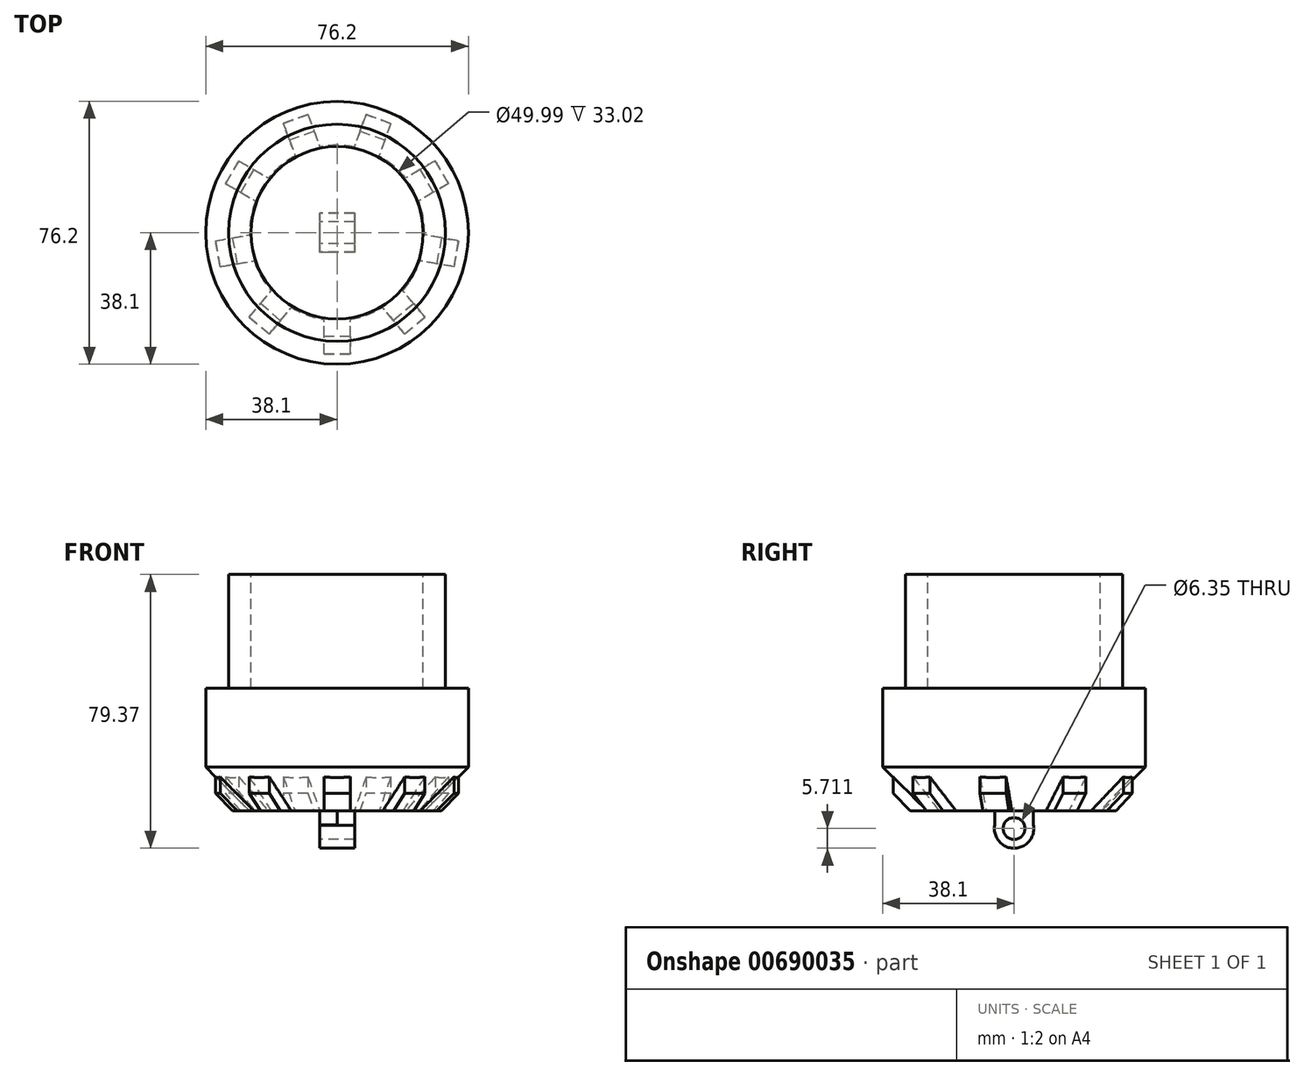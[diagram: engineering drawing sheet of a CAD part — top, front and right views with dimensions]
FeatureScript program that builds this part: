
annotation { "Feature Type Name" : "Feature", "Feature Type Description" : "" }
export const myFeature = defineFeature(function(context is Context, id is Id, definition is map)
    precondition{}
    {
        {
            var Q0;
            Q0=qCreatedBy(makeId("Top.planeOp"),FACE);
            cPlane(context, id + "F0", {"entities" : qUnion([Q0]), "cplaneType" : CPlaneType.OFFSET, "offset" : 83.28 * mm, "oppositeDirection" : true, "width" : 152.4 * mm, "height" : 152.4 * mm});
        }
        {
            var Q0;
            Q0=qCreatedBy(id+"F0.planeOp",FACE);
            cPlane(context, id + "F1", {"entities" : qUnion([Q0]), "cplaneType" : CPlaneType.OFFSET, "offset" : 15.6 * mm, "oppositeDirection" : true, "width" : 152.4 * mm, "height" : 152.4 * mm});
        }
        {
            var Q0;
            Q0=qCreatedBy(id+"F1.planeOp",FACE);
            var sketch = newSketch(context, id + "F2", { "sketchPlane" : qUnion([Q0])});
            skCircle(sketch, "E0", {"center": v(0, 0) * mm, "radius": 25 * mm});
            skCircle(sketch, "E1", {"center": v(0, 0) * mm, "radius": 31.46 * mm});
            skSolve(sketch);
        }
        {
            var Q0;
            Q0=makeQuery(id+"F2.imprint","IMPRINT",FACE,{"disambiguationData":[TD([[makeQuery(id+"F2.imprint","IMPRINT",EDGE,{"derivedFrom":sQuery(id+"F2.wireOp",EDGE,"E0")}),-1.0]])]});
            extrude(context, id + "F3", {"entities" : qUnion([Q0]), "oppositeDirection" : true, "depth" : 33.02 * mm, "offsetDistance" : 25.4 * mm});
        }
        {
            var Q0;
            Q0=makeQuery(id+"F3.opExtrude","CAP_FACE",FACE,{"disambiguationData":[OSD([sQuery(id+"F2.wireOp",EDGE,"E0"),sQuery(id+"F2.wireOp",EDGE,"E1")])],"isStart":false});
            var sketch = newSketch(context, id + "F4", { "sketchPlane" : qUnion([Q0])});
            skCircle(sketch, "E2", {"center": v(0, 0) * mm, "radius": 38.1 * mm});
            skSolve(sketch);
        }
        {
            var Q0;
            Q0=makeQuery(id+"F4.imprint","IMPRINT",FACE,{"disambiguationData":[TD([[makeQuery(id+"F4.imprint","IMPRINT",EDGE,{"derivedFrom":sQuery(id+"F4.wireOp",EDGE,"E2")}),1.0]])]});
            var Q1;
            Q1=makeQuery(id+"F4.imprint","IMPRINT",FACE,{"disambiguationData":[TD([[makeQuery(id+"F4.imprint","IMPRINT",EDGE,{"derivedFrom":makeQuery(id+"F3.opExtrude","CAP_EDGE",EDGE,{"disambiguationData":[OSD([sQuery(id+"F2.wireOp",EDGE,"E0")])],"isStart":false})}),1.0]])]});
            var Q2;
            Q2=makeQuery(id+"F4.imprint","IMPRINT",FACE,{"disambiguationData":[TD([[makeQuery(id+"F4.imprint","IMPRINT",EDGE,{"derivedFrom":makeQuery(id+"F3.opExtrude","CAP_EDGE",EDGE,{"disambiguationData":[OSD([sQuery(id+"F2.wireOp",EDGE,"E0")])],"isStart":false})}),-1.0]])]});
            extrude(context, id + "F5", {"entities" : qUnion([Q0, Q1, Q2]), "operationType" : NewBodyOperationType.ADD, "depth" : 35.56 * mm, "offsetDistance" : 25.4 * mm});
        }
        {
            var Q0;
            Q0=makeQuery(id+"F5.opExtrude","CAP_EDGE",EDGE,{"disambiguationData":[OSD([sQuery(id+"F4.wireOp",EDGE,"E2")])],"isStart":false});
            chamfer(context, id + "F6", {"entities" : qUnion([Q0]), "width" : 12.7 * mm, "tangentPropagation" : true});
        }
        {
            var Q0;
            Q0=makeQuery(id+"F5.opExtrude","CAP_FACE",FACE,{"disambiguationData":[OSD([sQuery(id+"F4.wireOp",EDGE,"E2")])],"isStart":false});
            var sketch = newSketch(context, id + "F7", { "sketchPlane" : qUnion([Q0])});
            skSolve(sketch);
        }
        {
            var Q0;
            {var subQ0=sQuery(id+"F4.wireOp",EDGE,"E2");Q0=makeQuery(id+"F7.imprint","IMPRINT",FACE,{"disambiguationData":[TD([[makeQuery(id+"F7.imprint","IMPRINT",EDGE,{"derivedFrom":makeQuery(id+"F6.opChamfer","BLEND_EDGE",EDGE,{"blendedFrom":[makeQuery(id+"F5.opExtrude","CAP_EDGE",EDGE,{"disambiguationData":[OSD([subQ0])],"isStart":false}),makeQuery(id+"F5.opExtrude","CAP_FACE",FACE,{"disambiguationData":[OSD([subQ0])],"isStart":false})],"blendedInto":[makeQuery(id+"F5.opExtrude","CAP_FACE",FACE,{"disambiguationData":[OSD([subQ0])],"isStart":false})]})}),1.0]])]});}
            var sketch = newSketch(context, id + "F8", { "sketchPlane" : qUnion([Q0])});
            skLineSegment(sketch, "E3.bottom", {"start": v(3.81, 23.68) * mm, "end": v(-3.81, 23.68) * mm});
            skLineSegment(sketch, "E3.top", {"start": v(3.81, 35.11) * mm, "end": v(-3.81, 35.11) * mm});
            skLineSegment(sketch, "E3.left", {"start": v(3.8, 35.11) * mm, "end": v(3.81, 23.68) * mm});
            skLineSegment(sketch, "E3.right", {"start": v(-3.81, 35.11) * mm, "end": v(-3.81, 23.68) * mm});
            skPoint(sketch, "E3.middle", {"position": v(0, 29.4) * mm});
            skLineSegment(sketch, "E4.1.0", {"start": v(-19.65, 29.35) * mm, "end": v(-12.3, 20.6) * mm});
            skPoint(sketch, "E4.1.1", {"position": v(-18.9, 22.52) * mm});
            skLineSegment(sketch, "E4.1.2", {"start": v(-19.65, 29.35) * mm, "end": v(-25.49, 24.45) * mm});
            skLineSegment(sketch, "E4.1.3", {"start": v(-25.49, 24.45) * mm, "end": v(-18.14, 15.7) * mm});
            skLineSegment(sketch, "E4.1.4", {"start": v(-12.3, 20.6) * mm, "end": v(-18.14, 15.7) * mm});
            skLineSegment(sketch, "E4.2.0", {"start": v(-33.92, 9.85) * mm, "end": v(-22.66, 7.86) * mm});
            skPoint(sketch, "E4.2.1", {"position": v(-28.95, 5.1) * mm});
            skLineSegment(sketch, "E4.2.2", {"start": v(-33.92, 9.85) * mm, "end": v(-35.24, 2.35) * mm});
            skLineSegment(sketch, "E4.2.3", {"start": v(-35.24, 2.35) * mm, "end": v(-23.98, 0.36) * mm});
            skLineSegment(sketch, "E4.2.4", {"start": v(-22.66, 7.86) * mm, "end": v(-23.98, 0.36) * mm});
            skLineSegment(sketch, "E4.3.0", {"start": v(-32.31, -14.26) * mm, "end": v(-22.42, -8.54) * mm});
            skPoint(sketch, "E4.3.1", {"position": v(-25.46, -14.7) * mm});
            skLineSegment(sketch, "E4.3.2", {"start": v(-32.31, -14.26) * mm, "end": v(-28.5, -20.86) * mm});
            skLineSegment(sketch, "E4.3.3", {"start": v(-28.5, -20.86) * mm, "end": v(-18.6, -15.14) * mm});
            skLineSegment(sketch, "E4.3.4", {"start": v(-22.42, -8.54) * mm, "end": v(-18.6, -15.14) * mm});
            skLineSegment(sketch, "E4.4.0", {"start": v(-15.59, -31.7) * mm, "end": v(-11.68, -20.95) * mm});
            skPoint(sketch, "E4.4.1", {"position": v(-10.05, -27.63) * mm});
            skLineSegment(sketch, "E4.4.2", {"start": v(-15.59, -31.7) * mm, "end": v(-8.43, -34.3) * mm});
            skLineSegment(sketch, "E4.4.3", {"start": v(-8.43, -34.3) * mm, "end": v(-4.52, -23.56) * mm});
            skLineSegment(sketch, "E4.4.4", {"start": v(-11.68, -20.95) * mm, "end": v(-4.52, -23.56) * mm});
            skLineSegment(sketch, "E4.5.0", {"start": v(8.43, -34.3) * mm, "end": v(4.52, -23.56) * mm});
            skPoint(sketch, "E4.5.1", {"position": v(10.05, -27.63) * mm});
            skLineSegment(sketch, "E4.5.2", {"start": v(8.43, -34.3) * mm, "end": v(15.59, -31.7) * mm});
            skLineSegment(sketch, "E4.5.3", {"start": v(15.59, -31.7) * mm, "end": v(11.68, -20.95) * mm});
            skLineSegment(sketch, "E4.5.4", {"start": v(4.52, -23.56) * mm, "end": v(11.68, -20.95) * mm});
            skLineSegment(sketch, "E4.6.0", {"start": v(28.5, -20.86) * mm, "end": v(18.6, -15.14) * mm});
            skPoint(sketch, "E4.6.1", {"position": v(25.46, -14.7) * mm});
            skLineSegment(sketch, "E4.6.2", {"start": v(28.5, -20.86) * mm, "end": v(32.31, -14.26) * mm});
            skLineSegment(sketch, "E4.6.3", {"start": v(32.31, -14.26) * mm, "end": v(22.42, -8.54) * mm});
            skLineSegment(sketch, "E4.6.4", {"start": v(18.6, -15.14) * mm, "end": v(22.42, -8.54) * mm});
            skLineSegment(sketch, "E4.7.0", {"start": v(35.24, 2.35) * mm, "end": v(23.98, 0.36) * mm});
            skPoint(sketch, "E4.7.1", {"position": v(28.95, 5.1) * mm});
            skLineSegment(sketch, "E4.7.2", {"start": v(35.24, 2.35) * mm, "end": v(33.92, 9.85) * mm});
            skLineSegment(sketch, "E4.7.3", {"start": v(33.92, 9.85) * mm, "end": v(22.66, 7.86) * mm});
            skLineSegment(sketch, "E4.7.4", {"start": v(23.98, 0.36) * mm, "end": v(22.66, 7.86) * mm});
            skLineSegment(sketch, "E4.8.0", {"start": v(25.49, 24.45) * mm, "end": v(18.14, 15.7) * mm});
            skPoint(sketch, "E4.8.1", {"position": v(18.9, 22.52) * mm});
            skLineSegment(sketch, "E4.8.2", {"start": v(25.49, 24.45) * mm, "end": v(19.65, 29.35) * mm});
            skLineSegment(sketch, "E4.8.3", {"start": v(19.65, 29.35) * mm, "end": v(12.3, 20.6) * mm});
            skLineSegment(sketch, "E4.8.4", {"start": v(18.14, 15.7) * mm, "end": v(12.3, 20.6) * mm});
            skPoint(sketch, "E4.center", {"position": v(0, 0) * mm});
            skSolve(sketch);
        }
        {
            var Q0;
            Q0 = qSketchRegion(id + "F8", true);
            extrude(context, id + "F9", {"entities" : qUnion([Q0]), "operationType" : NewBodyOperationType.ADD, "oppositeDirection" : true, "depth" : 15.76 * mm, "offsetDistance" : 25.4 * mm});
        }
        {
            var Q0;
            Q0=makeQuery(id+"F9.opExtrude","CAP_EDGE",EDGE,{"disambiguationData":[OSD([sQuery(id+"F8.wireOp",EDGE,"E4.2.2")])],"isStart":true});
            var Q1;
            Q1=makeQuery(id+"F9.opExtrude","CAP_EDGE",EDGE,{"disambiguationData":[OSD([sQuery(id+"F8.wireOp",EDGE,"E4.1.2")])],"isStart":true});
            var Q2;
            Q2=makeQuery(id+"F9.opExtrude","CAP_EDGE",EDGE,{"disambiguationData":[OSD([sQuery(id+"F8.wireOp",EDGE,"E3.top")])],"isStart":true});
            var Q3;
            Q3=makeQuery(id+"F9.opExtrude","CAP_EDGE",EDGE,{"disambiguationData":[OSD([sQuery(id+"F8.wireOp",EDGE,"E4.8.2")])],"isStart":true});
            var Q4;
            Q4=makeQuery(id+"F9.opExtrude","CAP_EDGE",EDGE,{"disambiguationData":[OSD([sQuery(id+"F8.wireOp",EDGE,"E4.7.2")])],"isStart":true});
            var Q5;
            Q5=makeQuery(id+"F9.opExtrude","CAP_EDGE",EDGE,{"disambiguationData":[OSD([sQuery(id+"F8.wireOp",EDGE,"E4.6.2")])],"isStart":true});
            var Q6;
            Q6=makeQuery(id+"F9.opExtrude","CAP_EDGE",EDGE,{"disambiguationData":[OSD([sQuery(id+"F8.wireOp",EDGE,"E4.5.2")])],"isStart":true});
            var Q7;
            Q7=makeQuery(id+"F9.opExtrude","CAP_EDGE",EDGE,{"disambiguationData":[OSD([sQuery(id+"F8.wireOp",EDGE,"E4.4.2")])],"isStart":true});
            var Q8;
            Q8=makeQuery(id+"F9.opExtrude","CAP_EDGE",EDGE,{"disambiguationData":[OSD([sQuery(id+"F8.wireOp",EDGE,"E4.3.2")])],"isStart":true});
            chamfer(context, id + "F10", {"entities" : qUnion([Q0, Q1, Q2, Q3, Q4, Q5, Q6, Q7, Q8]), "width" : 5.08 * mm, "tangentPropagation" : true});
        }
        {
            var Q0;
            Q0=qCreatedBy(makeId("Right.planeOp"),FACE);
            var sketch = newSketch(context, id + "F11", { "sketchPlane" : qUnion([Q0])});
            skCircle(sketch, "E5", {"center": v(0, -172.54) * mm, "radius": 3.18 * mm});
            skArc(sketch, "E6", {"start": v(-5.63, -171.56) * mm, "mid": v(0.04, -178.25) * mm, "end": v(5.62, -171.48) * mm});
            skLineSegment(sketch, "E7", {"start": v(5.62, -171.48) * mm, "end": v(5.62, -163.26) * mm});
            skLineSegment(sketch, "E8.MirrorCS", {"start": v(-5.63, -171.56) * mm, "end": v(-5.63, -163.26) * mm});
            skLineSegment(sketch, "E9", {"start": v(-5.63, -163.26) * mm, "end": v(5.62, -163.26) * mm});
            skSolve(sketch);
        }
        {
            var Q0;
            Q0=makeQuery(id+"F11.imprint","IMPRINT",FACE,{"disambiguationData":[TD([[makeQuery(id+"F11.imprint","IMPRINT",EDGE,{"derivedFrom":sQuery(id+"F11.wireOp",EDGE,"E5")}),-1.0]])]});
            extrude(context, id + "F12", {"entities" : qUnion([Q0]), "operationType" : NewBodyOperationType.ADD, "depth" : 5.08 * mm, "offsetDistance" : 25.4 * mm});
        }
        {
            var Q0;
            Q0=makeQuery(id+"F11.imprint","IMPRINT",FACE,{"disambiguationData":[TD([[makeQuery(id+"F11.imprint","IMPRINT",EDGE,{"derivedFrom":sQuery(id+"F11.wireOp",EDGE,"E5")}),-1.0]])]});
            var sketch = newSketch(context, id + "F13", { "sketchPlane" : qUnion([Q0])});
            skCircle(sketch, "E10", {"center": v(0, -172.54) * mm, "radius": 3.18 * mm});
            skArc(sketch, "E11", {"start": v(-5.62, -171.46) * mm, "mid": v(0, -178.26) * mm, "end": v(5.62, -171.46) * mm});
            skLineSegment(sketch, "E12", {"start": v(5.62, -171.46) * mm, "end": v(5.62, -163.56) * mm});
            skLineSegment(sketch, "E13", {"start": v(5.62, -163.56) * mm, "end": v(-5.72, -163.56) * mm});
            skLineSegment(sketch, "E14.MirrorCS", {"start": v(-5.62, -171.46) * mm, "end": v(-5.62, -163.56) * mm});
            skSolve(sketch);
        }
        {
            var Q0;
            Q0=makeQuery(id+"F13.imprint","IMPRINT",FACE,{"disambiguationData":[TD([[makeQuery(id+"F13.imprint","IMPRINT",EDGE,{"derivedFrom":sQuery(id+"F13.wireOp",EDGE,"E10")}),-1.0]])]});
            extrude(context, id + "F14", {"entities" : qUnion([Q0]), "operationType" : NewBodyOperationType.ADD, "oppositeDirection" : true, "depth" : 5.08 * mm, "offsetDistance" : 25.4 * mm});
        }
    });
